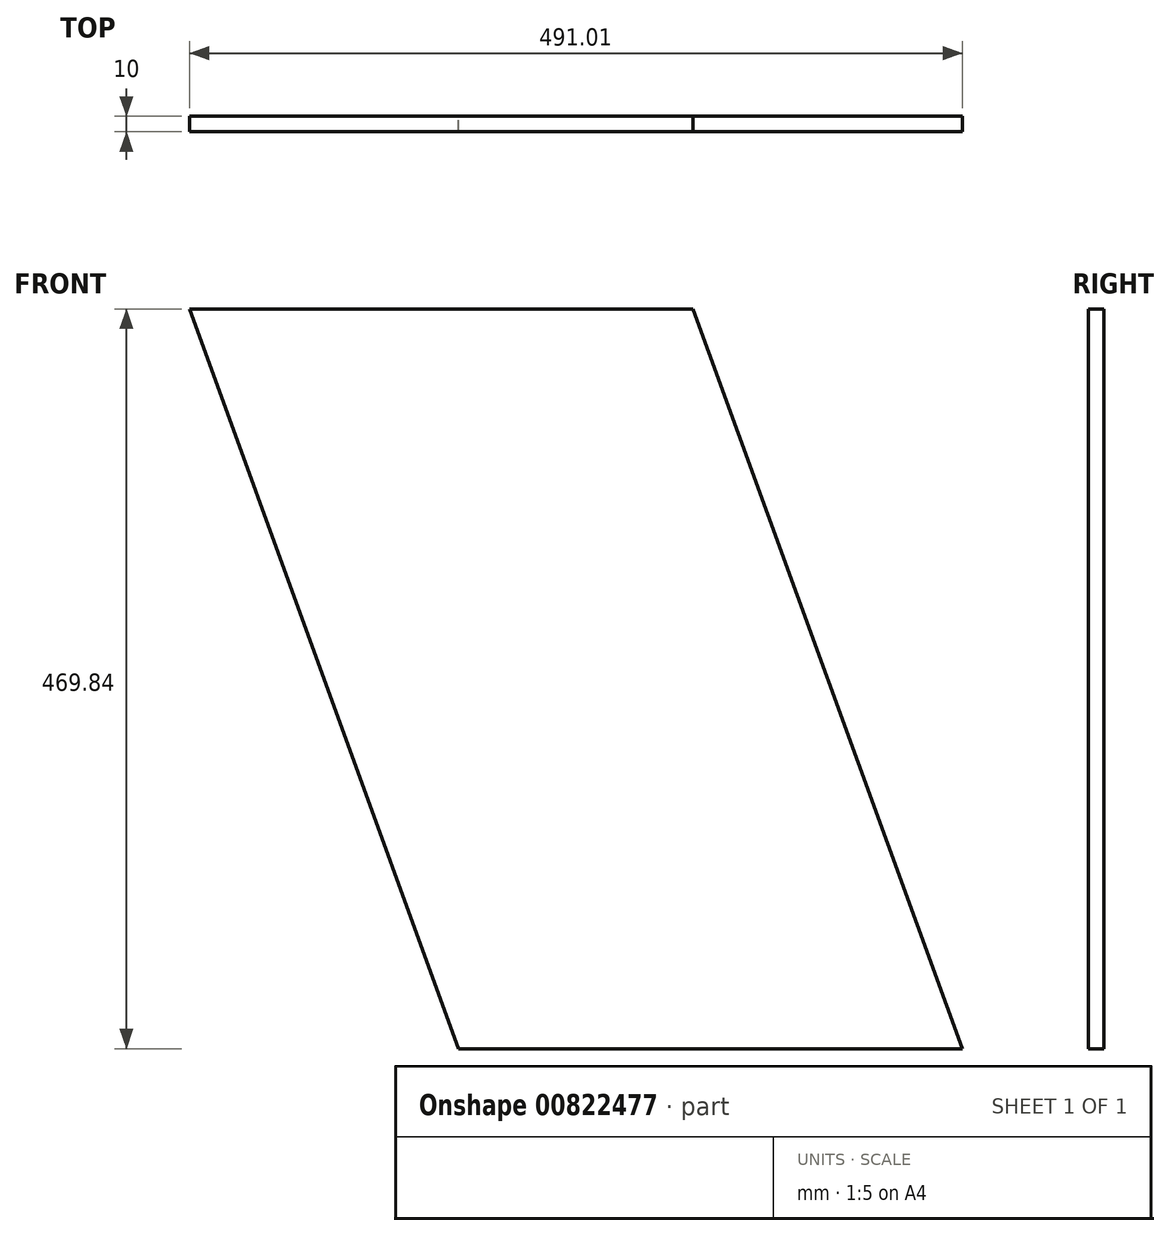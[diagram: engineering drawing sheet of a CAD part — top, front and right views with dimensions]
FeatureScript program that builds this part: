
annotation { "Feature Type Name" : "Feature", "Feature Type Description" : "" }
export const myFeature = defineFeature(function(context is Context, id is Id, definition is map)
    precondition{}
    {
        {
            var Q0;
            Q0=qCreatedBy(makeId("Front.planeOp"),FACE);
            var sketch = newSketch(context, id + "F0", { "sketchPlane" : qUnion([Q0])});
            skLineSegment(sketch, "E0", {"start": v(-93.66, -228.47) * mm, "end": v(-413.66, -228.47) * mm});
            skLineSegment(sketch, "E1", {"start": v(-413.66, -228.47) * mm, "end": v(-584.67, 241.37) * mm});
            skLineSegment(sketch, "E2", {"start": v(-584.67, 241.37) * mm, "end": v(-264.67, 241.37) * mm});
            skLineSegment(sketch, "E3", {"start": v(-264.67, 241.37) * mm, "end": v(-93.66, -228.47) * mm});
            skSolve(sketch);
        }
        {
            var Q0;
            Q0=makeQuery(id+"F0.imprint","IMPRINT",FACE,{"disambiguationData":[TD([[makeQuery(id+"F0.imprint","IMPRINT",EDGE,{"derivedFrom":sQuery(id+"F0.wireOp",EDGE,"E0")}),-1.0]])]});
            extrude(context, id + "F1", {"entities" : qUnion([Q0]), "depth" : 10 * mm, "offsetDistance" : 25.4 * mm});
        }
    });
